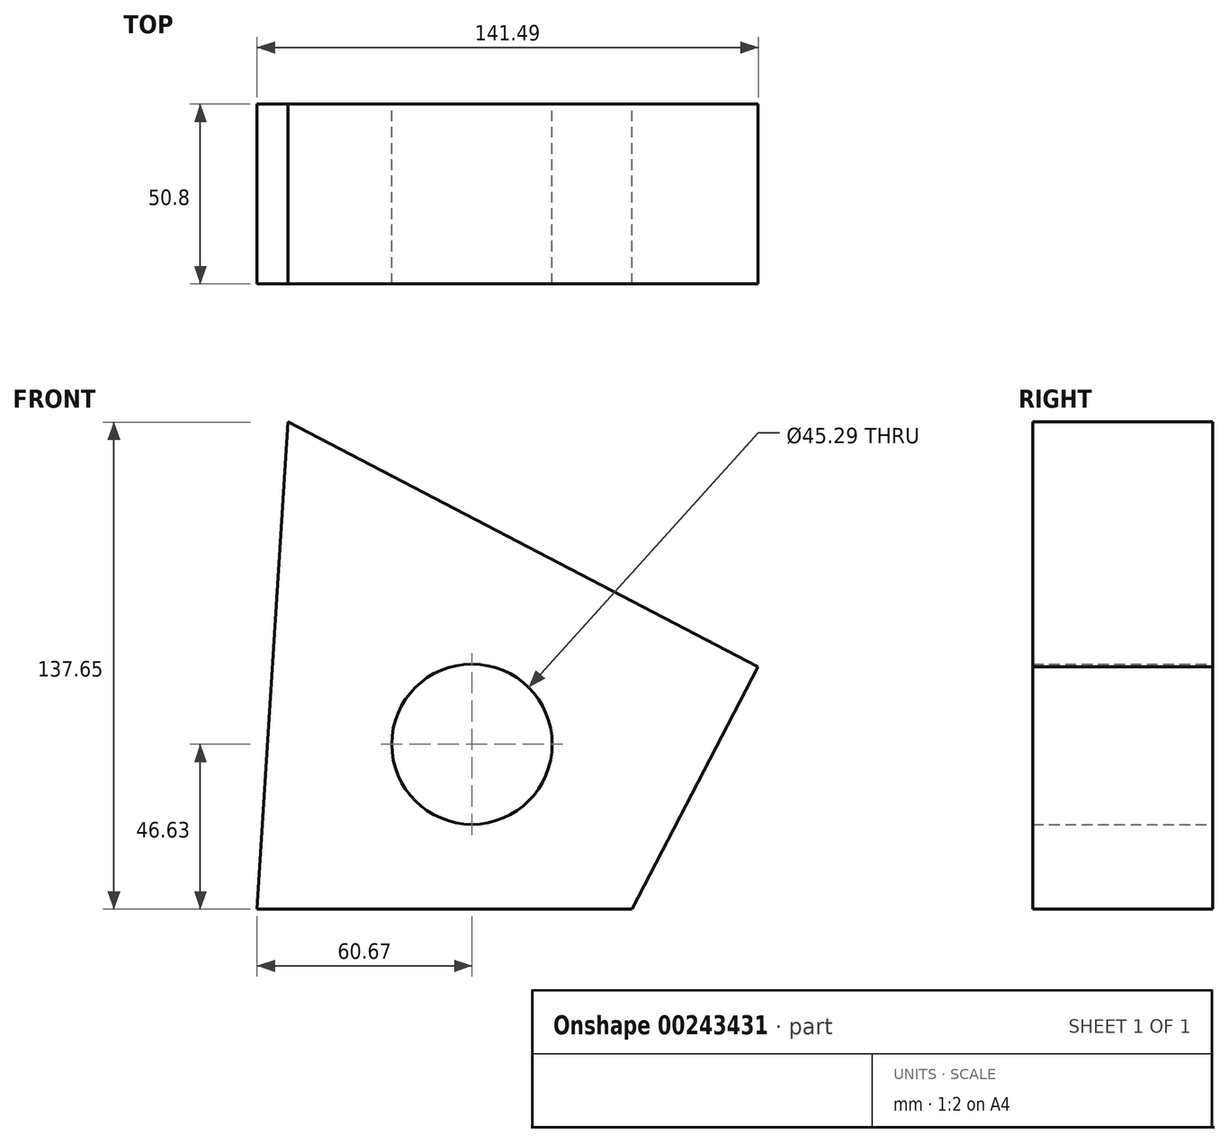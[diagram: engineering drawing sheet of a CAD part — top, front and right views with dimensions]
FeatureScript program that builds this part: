
annotation { "Feature Type Name" : "Feature", "Feature Type Description" : "" }
export const myFeature = defineFeature(function(context is Context, id is Id, definition is map)
    precondition{}
    {
        {
            var Q0;
            Q0=qCreatedBy(makeId("Front.planeOp"),FACE);
            var sketch = newSketch(context, id + "F0", { "sketchPlane" : qUnion([Q0])});
            skLineSegment(sketch, "E0", {"start": v(-51.98, 91.02) * mm, "end": v(80.82, 21.91) * mm});
            skLineSegment(sketch, "E1", {"start": v(-51.98, 91.02) * mm, "end": v(-60.67, -46.63) * mm});
            skLineSegment(sketch, "E2", {"start": v(-60.67, -46.63) * mm, "end": v(45.14, -46.63) * mm});
            skLineSegment(sketch, "E3", {"start": v(80.82, 21.91) * mm, "end": v(45.14, -46.63) * mm});
            skSolve(sketch);
        }
        {
            var Q0;
            Q0=makeQuery(id+"F0.imprint","IMPRINT",FACE,{"disambiguationData":[TD([[makeQuery(id+"F0.imprint","IMPRINT",EDGE,{"derivedFrom":sQuery(id+"F0.wireOp",EDGE,"E0")}),-1.0]])]});
            extrude(context, id + "F1", {"entities" : qUnion([Q0]), "depth" : 50.8 * mm});
        }
        {
            var Q0;
            Q0=makeQuery(id+"F1.opExtrude","CAP_FACE",FACE,{"disambiguationData":[OSD([sQuery(id+"F0.wireOp",EDGE,"E0"),sQuery(id+"F0.wireOp",EDGE,"E1"),sQuery(id+"F0.wireOp",EDGE,"E2"),sQuery(id+"F0.wireOp",EDGE,"E3")])],"isStart":true});
            var sketch = newSketch(context, id + "F2", { "sketchPlane" : qUnion([Q0])});
            skCircle(sketch, "E4", {"center": v(0, 0) * mm, "radius": 22.64 * mm});
            skSolve(sketch);
        }
        {
            var Q0;
            Q0=makeQuery(id+"F2.imprint","IMPRINT",FACE,{"disambiguationData":[TD([[makeQuery(id+"F2.imprint","IMPRINT",EDGE,{"derivedFrom":sQuery(id+"F2.wireOp",EDGE,"E4")}),1.0]])]});
            extrude(context, id + "F3", {"entities" : qUnion([Q0]), "operationType" : NewBodyOperationType.REMOVE, "oppositeDirection" : true, "depth" : 127 * mm});
        }
    });
